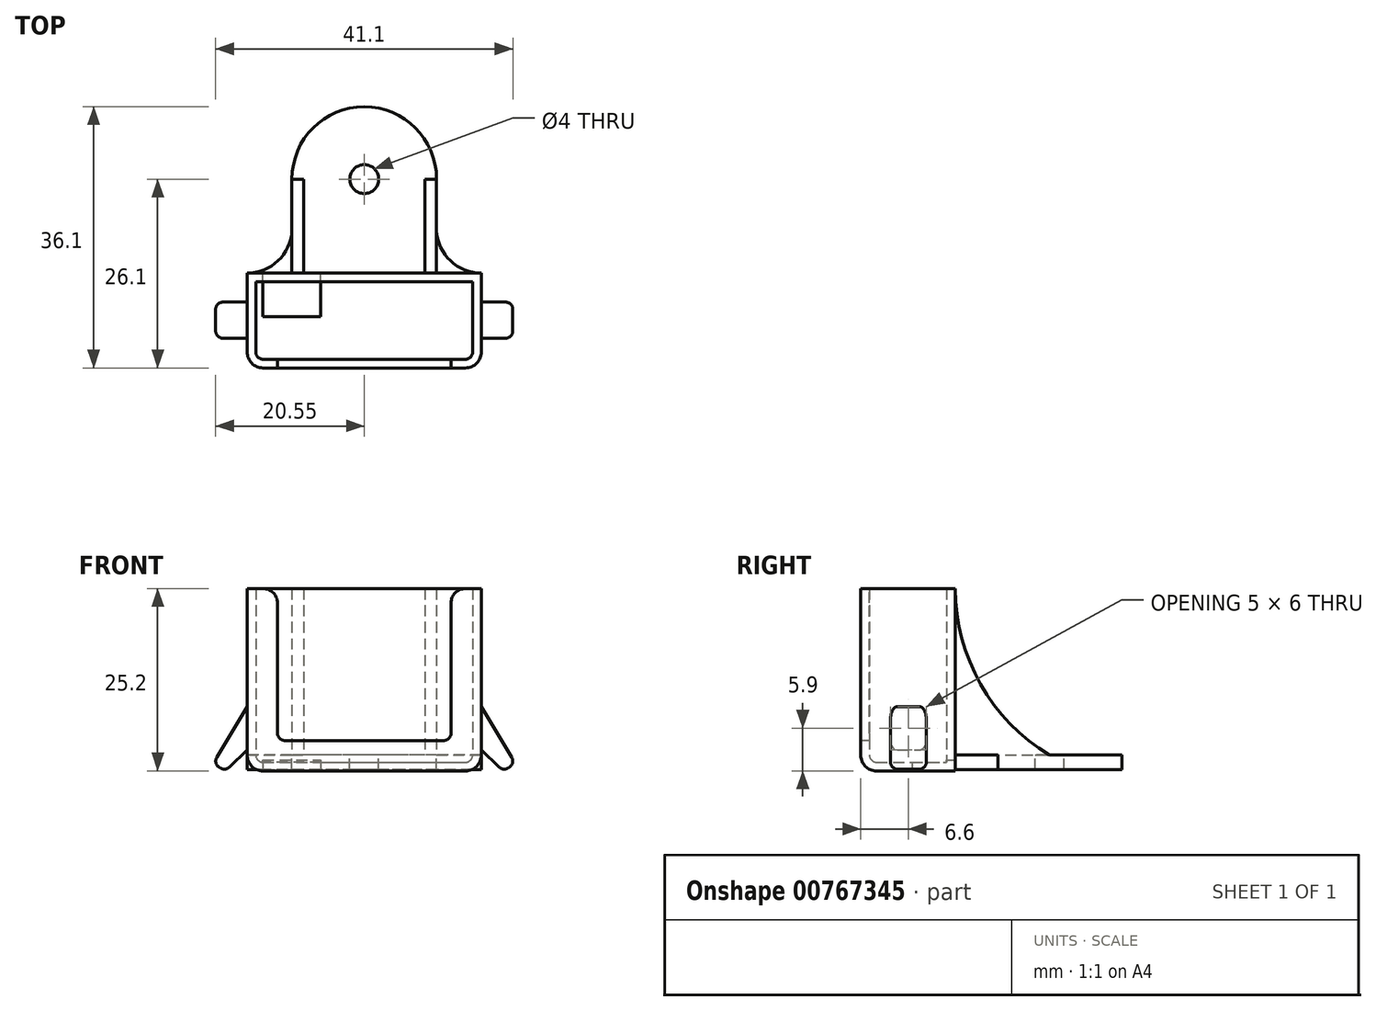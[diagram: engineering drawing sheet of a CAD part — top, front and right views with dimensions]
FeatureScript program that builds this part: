
annotation { "Feature Type Name" : "Feature", "Feature Type Description" : "" }
export const myFeature = defineFeature(function(context is Context, id is Id, definition is map)
    precondition{}
    {
        {
            var Q0;
            Q0=qCreatedBy(makeId("Front.planeOp"),FACE);
            var sketch = newSketch(context, id + "F0", { "sketchPlane" : qUnion([Q0])});
            skLineSegment(sketch, "E0.bottom", {"start": v(-15, 5) * mm, "end": v(15, 5) * mm});
            skLineSegment(sketch, "E0.top", {"start": v(-15, -20) * mm, "end": v(15, -20) * mm});
            skLineSegment(sketch, "E0.left", {"start": v(-15, 5) * mm, "end": v(-15, -20) * mm});
            skLineSegment(sketch, "E0.right", {"start": v(15, 5) * mm, "end": v(15, -20) * mm});
            skPoint(sketch, "E0.middle", {"position": v(0, -7.5) * mm});
            skPoint(sketch, "E1.visualSharp", {"position": v(-15, 5) * mm});
            skSolve(sketch);
        }
        {
            var Q0;
            Q0=qSketchRegion(id+"F0",true);
            extrude(context, id + "F1", {"entities" : qUnion([Q0]), "depth" : 10.7 * mm, "offsetDistance" : 25 * mm});
        }
        {
            var Q0;
            Q0=makeQuery(id+"F1.opExtrude","SWEPT_EDGE",EDGE,{"disambiguationData":[OSD([sQuery(id+"F0.wireOp",EDGE,"E0.bottom"),sQuery(id+"F0.wireOp",EDGE,"E0.right")])]});
            var Q1;
            Q1=makeQuery(id+"F1.opExtrude","SWEPT_EDGE",EDGE,{"disambiguationData":[OSD([sQuery(id+"F0.wireOp",EDGE,"E0.bottom"),sQuery(id+"F0.wireOp",EDGE,"E0.left")])]});
            var Q2;
            Q2=makeQuery(id+"F1.opExtrude","SWEPT_EDGE",EDGE,{"disambiguationData":[OSD([sQuery(id+"F0.wireOp",EDGE,"E0.top"),sQuery(id+"F0.wireOp",EDGE,"E0.left")])]});
            var Q3;
            Q3=makeQuery(id+"F1.opExtrude","SWEPT_EDGE",EDGE,{"disambiguationData":[OSD([sQuery(id+"F0.wireOp",EDGE,"E0.top"),sQuery(id+"F0.wireOp",EDGE,"E0.right")])]});
            var Q4;
            Q4=makeQuery(id+"F1.opExtrude","CAP_FACE",FACE,{"disambiguationData":[OSD([sQuery(id+"F0.wireOp",EDGE,"E0.bottom"),sQuery(id+"F0.wireOp",EDGE,"E0.top"),sQuery(id+"F0.wireOp",EDGE,"E0.left"),sQuery(id+"F0.wireOp",EDGE,"E0.right")])],"isStart":false});
            fillet(context, id + "F2", {"entities" : qUnion([Q0, Q1, Q2, Q3, Q4]), "radius" : 1 * mm, "tangentPropagation" : true, "allowEdgeOverflow" : false});
        }
        {
            var Q0;
            Q0=makeQuery(id+"F1.opExtrude","SWEPT_FACE",FACE,{"disambiguationData":[OSD([sQuery(id+"F0.wireOp",EDGE,"E0.bottom")])]});
            var Q1;
            Q1=makeQuery(id+"F2.opFillet","BLEND_FACE",FACE,{"disambiguationData":[OSD([sQuery(id+"F0.wireOp",EDGE,"E0.bottom")])]});
            shell(context, id + "F3", {"entities" : qUnion([Q0, Q1]), "thickness" : 1.2 * mm, "oppositeDirection" : true});
        }
        {
            var Q0;
            Q0=makeQuery(id+"F1.opExtrude","CAP_FACE",FACE,{"disambiguationData":[OSD([sQuery(id+"F0.wireOp",EDGE,"E0.bottom"),sQuery(id+"F0.wireOp",EDGE,"E0.top"),sQuery(id+"F0.wireOp",EDGE,"E0.left"),sQuery(id+"F0.wireOp",EDGE,"E0.right")])],"isStart":false});
            var sketch = newSketch(context, id + "F4", { "sketchPlane" : qUnion([Q0])});
            skLineSegment(sketch, "E2.bottom", {"start": v(-11, -17) * mm, "end": v(11, -17) * mm});
            skLineSegment(sketch, "E2.top", {"start": v(-12, 15) * mm, "end": v(12, 15) * mm});
            skLineSegment(sketch, "E2.left", {"start": v(-12, -16) * mm, "end": v(-12, 15) * mm});
            skLineSegment(sketch, "E2.right", {"start": v(12, -16) * mm, "end": v(12, 15) * mm});
            skPoint(sketch, "E3.visualSharp", {"position": v(-12, -17) * mm});
            skArc(sketch, "E3.filletArc", {"start": v(-12, -16) * mm, "mid": v(-11.7, -16.7) * mm, "end": v(-11, -17) * mm});
            skPoint(sketch, "E4.visualSharp", {"position": v(12, -17) * mm});
            skArc(sketch, "E4.filletArc", {"start": v(11, -17) * mm, "mid": v(11.7, -16.7) * mm, "end": v(12, -16) * mm});
            skLineSegment(sketch, "E5.bottom", {"start": v(-16.5, 7.5) * mm, "end": v(16.5, 7.5) * mm});
            skLineSegment(sketch, "E5.top", {"start": v(-16.5, 4) * mm, "end": v(16.5, 4) * mm});
            skLineSegment(sketch, "E5.left", {"start": v(-16.5, 7.5) * mm, "end": v(-16.5, 4) * mm});
            skLineSegment(sketch, "E5.right", {"start": v(16.5, 7.5) * mm, "end": v(16.5, 4) * mm});
            skSolve(sketch);
        }
        {
            var Q0;
            Q0=makeQuery(id+"F4.imprint","IMPRINT",FACE,{"disambiguationData":[TD([[makeQuery(id+"F4.imprint","IMPRINT",EDGE,{"derivedFrom":sQuery(id+"F4.wireOp",EDGE,"E2.bottom")}),1.0]])]});
            var Q1;
            {var subQ0=sQuery(id+"F4.wireOp",EDGE,"E5.bottom");var subQ1=sQuery(id+"F4.wireOp",EDGE,"E2.left");var subQ2=makeQuery(id+"F4.imprint","INTERSECT",VERTEX,{"derivedFrom":[subQ1,subQ0]});Q1=makeQuery(id+"F4.imprint","IMPRINT",FACE,{"disambiguationData":[TD([[makeQuery(id+"F4.imprint","IMPRINT",EDGE,{"disambiguationData":[TD([[subQ2,1.0]])],"derivedFrom":subQ1}),-1.0]])]});}
            var Q2;
            {var subQ0=sQuery(id+"F4.wireOp",EDGE,"E2.top");Q2=makeQuery(id+"F4.imprint","IMPRINT",FACE,{"disambiguationData":[TD([[makeQuery(id+"F4.imprint","IMPRINT",EDGE,{"derivedFrom":subQ0}),-1.0]])]});}
            extrude(context, id + "F5", {"entities" : qUnion([Q0, Q1, Q2]), "operationType" : NewBodyOperationType.REMOVE, "oppositeDirection" : true, "depth" : 3 * mm, "offsetDistance" : 25 * mm});
        }
        {
            var Q0;
            {var subQ8=sQuery(id+"F4.wireOp",EDGE,"E5.left");Q0=makeQuery(id+"F4.imprint","IMPRINT",FACE,{"disambiguationData":[TD([[makeQuery(id+"F4.imprint","IMPRINT",EDGE,{"derivedFrom":subQ8}),1.0]])]});}
            var Q1;
            {var subQ0=sQuery(id+"F4.wireOp",EDGE,"E5.bottom");var subQ1=sQuery(id+"F4.wireOp",EDGE,"E2.left");var subQ2=makeQuery(id+"F4.imprint","INTERSECT",VERTEX,{"derivedFrom":[subQ1,subQ0]});Q1=makeQuery(id+"F4.imprint","IMPRINT",FACE,{"disambiguationData":[TD([[makeQuery(id+"F4.imprint","IMPRINT",EDGE,{"disambiguationData":[TD([[subQ2,1.0]])],"derivedFrom":subQ1}),-1.0]])]});}
            var Q2;
            {var subQ6=sQuery(id+"F4.wireOp",EDGE,"E5.right");Q2=makeQuery(id+"F4.imprint","IMPRINT",FACE,{"disambiguationData":[TD([[makeQuery(id+"F4.imprint","IMPRINT",EDGE,{"derivedFrom":subQ6}),-1.0]])]});}
            extrude(context, id + "F6", {"entities" : qUnion([Q0, Q1, Q2]), "operationType" : NewBodyOperationType.REMOVE, "oppositeDirection" : true, "depth" : 25 * mm, "offsetDistance" : 25 * mm});
        }
        {
            var Q0;
            {var subQ0=sQuery(id+"F0.wireOp",EDGE,"E0.right");var subQ1=sQuery(id+"F0.wireOp",EDGE,"E0.left");var subQ2=sQuery(id+"F0.wireOp",EDGE,"E0.top");var subQ3=sQuery(id+"F0.wireOp",EDGE,"E0.bottom");Q0=makeQuery(id+"F5.boolean.opBoolean","INTERSECT",EDGE,{"derivedFrom":[makeQuery(id+"F3.opShell","OFFSET_FACE",FACE,{"disambiguationData":[OSD([subQ3,subQ2,subQ1,subQ0]),TDD([makeQuery(id+"F2.opFillet","BLEND_EDGE",EDGE,{"blendedFrom":[makeQuery(id+"F1.opExtrude","CAP_EDGE",EDGE,{"disambiguationData":[OSD([subQ3])],"isStart":false}),makeQuery(id+"F1.opExtrude","CAP_FACE",FACE,{"disambiguationData":[OSD([subQ3,subQ2,subQ1,subQ0])],"isStart":false})],"blendedInto":[makeQuery(id+"F1.opExtrude","CAP_FACE",FACE,{"disambiguationData":[OSD([subQ3,subQ2,subQ1,subQ0])],"isStart":false})]})])]}),makeQuery(id+"F5.opExtrude","SWEPT_FACE",FACE,{"disambiguationData":[OSD([sQuery(id+"F4.wireOp",EDGE,"E2.right")])]})]});}
            var Q1;
            {var subQ0=sQuery(id+"F0.wireOp",EDGE,"E0.right");var subQ1=sQuery(id+"F0.wireOp",EDGE,"E0.left");var subQ2=sQuery(id+"F0.wireOp",EDGE,"E0.top");var subQ3=sQuery(id+"F0.wireOp",EDGE,"E0.bottom");Q1=makeQuery(id+"F5.boolean.opBoolean","INTERSECT",EDGE,{"derivedFrom":[makeQuery(id+"F3.opShell","OFFSET_FACE",FACE,{"disambiguationData":[OSD([subQ3,subQ2,subQ1,subQ0]),TDD([makeQuery(id+"F2.opFillet","BLEND_EDGE",EDGE,{"blendedFrom":[makeQuery(id+"F1.opExtrude","CAP_EDGE",EDGE,{"disambiguationData":[OSD([subQ3])],"isStart":false}),makeQuery(id+"F1.opExtrude","CAP_FACE",FACE,{"disambiguationData":[OSD([subQ3,subQ2,subQ1,subQ0])],"isStart":false})],"blendedInto":[makeQuery(id+"F1.opExtrude","CAP_FACE",FACE,{"disambiguationData":[OSD([subQ3,subQ2,subQ1,subQ0])],"isStart":false})]})])]}),makeQuery(id+"F5.opExtrude","SWEPT_FACE",FACE,{"disambiguationData":[OSD([sQuery(id+"F4.wireOp",EDGE,"E2.left")])]})]});}
            fillet(context, id + "F7", {"entities" : qUnion([Q0, Q1]), "radius" : 2 * mm, "tangentPropagation" : true, "allowEdgeOverflow" : false});
        }
        {
            var Q0;
            Q0=makeQuery(id+"F1.opExtrude","CAP_FACE",FACE,{"disambiguationData":[OSD([sQuery(id+"F0.wireOp",EDGE,"E0.bottom"),sQuery(id+"F0.wireOp",EDGE,"E0.top"),sQuery(id+"F0.wireOp",EDGE,"E0.left"),sQuery(id+"F0.wireOp",EDGE,"E0.right")])],"isStart":true});
            var sketch = newSketch(context, id + "F8", { "sketchPlane" : qUnion([Q0])});
            skLineSegment(sketch, "E6.bottom", {"start": v(6, -19.7) * mm, "end": v(14, -19.7) * mm});
            skLineSegment(sketch, "E6.top", {"start": v(6, -24.7) * mm, "end": v(14, -24.7) * mm});
            skLineSegment(sketch, "E6.left", {"start": v(6, -19.7) * mm, "end": v(6, -24.7) * mm});
            skLineSegment(sketch, "E6.right", {"start": v(14, -19.7) * mm, "end": v(14, -24.7) * mm});
            skSolve(sketch);
        }
        {
            var Q0;
            Q0=qSketchRegion(id+"F8",true);
            extrude(context, id + "F9", {"entities" : qUnion([Q0]), "operationType" : NewBodyOperationType.REMOVE, "oppositeDirection" : true, "depth" : 6 * mm, "offsetDistance" : 25 * mm});
        }
        {
            var Q0;
            Q0=qCreatedBy(makeId("Top.planeOp"),FACE);
            var sketch = newSketch(context, id + "F10", { "sketchPlane" : qUnion([Q0])});
            skLineSegment(sketch, "E7.bottom", {"start": v(-10, 1.2) * mm, "end": v(10, 1.2) * mm});
            skLineSegment(sketch, "E7.top", {"start": v(0, 24.2) * mm, "end": v(0, 24.2) * mm});
            skLineSegment(sketch, "E7.left", {"start": v(-10, 1.2) * mm, "end": v(-10, 14.2) * mm});
            skLineSegment(sketch, "E7.right", {"start": v(10, 1.2) * mm, "end": v(10, 14.2) * mm});
            skPoint(sketch, "E8.visualSharp", {"position": v(-10, 24.2) * mm});
            skArc(sketch, "E8.filletArc", {"start": v(0, 24.2) * mm, "mid": v(-7.07, 21.27) * mm, "end": v(-10, 14.2) * mm});
            skPoint(sketch, "E9.visualSharp", {"position": v(10, 24.2) * mm});
            skArc(sketch, "E9.filletArc", {"start": v(10, 14.2) * mm, "mid": v(7.07, 21.27) * mm, "end": v(0, 24.2) * mm});
            skCircle(sketch, "E10", {"center": v(0, 14.2) * mm, "radius": 2 * mm});
            skLineSegment(sketch, "E11", {"start": v(-10, 1.2) * mm, "end": v(-16.2, 1.2) * mm});
            skLineSegment(sketch, "E12", {"start": v(10, 1.2) * mm, "end": v(16.2, 1.2) * mm});
            skArc(sketch, "E13", {"start": v(-16.2, 1.2) * mm, "mid": v(-11.7, 3.12) * mm, "end": v(-10, 7.7) * mm});
            skArc(sketch, "E14", {"start": v(10, 7.7) * mm, "mid": v(11.7, 3.12) * mm, "end": v(16.2, 1.2) * mm});
            skSolve(sketch);
        }
        {
            var Q0;
            Q0=qSketchRegion(id+"F10",true);
            extrude(context, id + "F11", {"entities" : qUnion([Q0]), "operationType" : NewBodyOperationType.ADD, "oppositeDirection" : true, "depth" : 21 * mm, "offsetDistance" : 25 * mm, "hasSecondDirection" : true, "secondDirectionOppositeDirection" : true, "secondDirectionDepth" : 19 * mm});
        }
        {
            var Q0;
            {var subQ2=sQuery(id+"F0.wireOp",EDGE,"E0.right");var subQ3=sQuery(id+"F0.wireOp",EDGE,"E0.top");var subQ4=sQuery(id+"F0.wireOp",EDGE,"E0.left");Q0=makeQuery(id+"F11.boolean.opBoolean","SPLIT",FACE,{"disambiguationData":[TD([makeQuery(id+"F1.opExtrude","SWEPT_FACE",FACE,{"disambiguationData":[OSD([subQ3])]})])],"derivedFrom":makeQuery(id+"F1.opExtrude","CAP_FACE",FACE,{"disambiguationData":[OSD([sQuery(id+"F0.wireOp",EDGE,"E0.bottom"),subQ3,subQ4,subQ2])],"isStart":true})});}
            var sketch = newSketch(context, id + "F12", { "sketchPlane" : qUnion([Q0])});
            skLineSegment(sketch, "E15", {"start": v(16.2, -12.3) * mm, "end": v(20.4, -19.33) * mm});
            skLineSegment(sketch, "E16", {"start": v(20.06, -20.7) * mm, "end": v(19.86, -20.82) * mm});
            skLineSegment(sketch, "E17", {"start": v(18.65, -20.68) * mm, "end": v(16.2, -18.3) * mm});
            skLineSegment(sketch, "E18", {"start": v(16.2, -18.3) * mm, "end": v(16.2, -12.3) * mm});
            skPoint(sketch, "E19.visualSharp", {"position": v(20.92, -20.2) * mm});
            skArc(sketch, "E19.filletArc", {"start": v(20.06, -20.7) * mm, "mid": v(20.52, -20.1) * mm, "end": v(20.4, -19.33) * mm});
            skPoint(sketch, "E20.visualSharp", {"position": v(19.2, -21.22) * mm});
            skArc(sketch, "E20.filletArc", {"start": v(18.65, -20.68) * mm, "mid": v(19.23, -20.96) * mm, "end": v(19.86, -20.82) * mm});
            skLineSegment(sketch, "E21.MirrorCS", {"start": v(-20.06, -20.7) * mm, "end": v(-19.86, -20.82) * mm});
            skArc(sketch, "E22.MirrorCS", {"start": v(-20.06, -20.7) * mm, "mid": v(-20.52, -20.1) * mm, "end": v(-20.4, -19.33) * mm});
            skArc(sketch, "E23.MirrorCS", {"start": v(-18.65, -20.68) * mm, "mid": v(-19.23, -20.96) * mm, "end": v(-19.86, -20.82) * mm});
            skPoint(sketch, "E24.MirrorP", {"position": v(-20.92, -20.2) * mm});
            skPoint(sketch, "E25.MirrorP", {"position": v(-19.2, -21.22) * mm});
            skLineSegment(sketch, "E26.MirrorCS", {"start": v(-16.2, -18.3) * mm, "end": v(-16.2, -12.3) * mm});
            skLineSegment(sketch, "E27.MirrorCS", {"start": v(-18.65, -20.68) * mm, "end": v(-16.2, -18.3) * mm});
            skLineSegment(sketch, "E28.MirrorCS", {"start": v(-16.2, -12.3) * mm, "end": v(-20.4, -19.33) * mm});
            skSolve(sketch);
        }
        {
            var Q0;
            Q0=qSketchRegion(id+"F12",true);
            extrude(context, id + "F13", {"entities" : qUnion([Q0]), "operationType" : NewBodyOperationType.ADD, "oppositeDirection" : true, "depth" : 9 * mm, "offsetDistance" : 25 * mm, "hasSecondDirection" : true, "secondDirectionOppositeDirection" : true, "secondDirectionDepth" : 4 * mm});
        }
        {
            var Q0;
            Q0=makeQuery(id+"F13.opExtrude","CAP_EDGE",EDGE,{"disambiguationData":[OSD([sQuery(id+"F12.wireOp",EDGE,"E15")])],"isStart":true});
            var Q1;
            Q1=makeQuery(id+"F13.opExtrude","CAP_EDGE",EDGE,{"disambiguationData":[OSD([sQuery(id+"F12.wireOp",EDGE,"E15")])],"isStart":false});
            var Q2;
            Q2=makeQuery(id+"F13.opExtrude","CAP_EDGE",EDGE,{"disambiguationData":[OSD([sQuery(id+"F12.wireOp",EDGE,"E28.MirrorCS")])],"isStart":false});
            var Q3;
            Q3=makeQuery(id+"F13.opExtrude","CAP_EDGE",EDGE,{"disambiguationData":[OSD([sQuery(id+"F12.wireOp",EDGE,"E28.MirrorCS")])],"isStart":true});
            fillet(context, id + "F14", {"entities" : qUnion([Q0, Q1, Q2, Q3]), "radius" : 1 * mm, "tangentPropagation" : true, "allowEdgeOverflow" : false});
        }
        {
            var Q0;
            Q0=qCreatedBy(makeId("Right.planeOp"),FACE);
            var sketch = newSketch(context, id + "F15", { "sketchPlane" : qUnion([Q0])});
            skArc(sketch, "E29", {"start": v(1.2, 4) * mm, "mid": v(4.67, -9.2) * mm, "end": v(14.2, -19) * mm});
            skLineSegment(sketch, "E30", {"start": v(1.2, 4) * mm, "end": v(1.2, -19) * mm});
            skLineSegment(sketch, "E31", {"start": v(1.2, -19) * mm, "end": v(14.2, -19) * mm});
            skSolve(sketch);
        }
        {
            var Q0;
            Q0=makeQuery(id+"F15.imprint","IMPRINT",FACE,{"disambiguationData":[TD([[makeQuery(id+"F15.imprint","IMPRINT",EDGE,{"derivedFrom":sQuery(id+"F15.wireOp",EDGE,"E29")}),-1.0]])]});
            extrude(context, id + "F16", {"entities" : qUnion([Q0]), "operationType" : NewBodyOperationType.ADD, "depth" : 10 * mm, "offsetDistance" : 25 * mm, "hasSecondDirection" : true, "secondDirectionOppositeDirection" : false, "secondDirectionDepth" : 8.4 * mm});
        }
        {
            var Q0;
            Q0=makeQuery(id+"F15.imprint","IMPRINT",FACE,{"disambiguationData":[TD([[makeQuery(id+"F15.imprint","IMPRINT",EDGE,{"derivedFrom":sQuery(id+"F15.wireOp",EDGE,"E29")}),-1.0]])]});
            extrude(context, id + "F17", {"entities" : qUnion([Q0]), "operationType" : NewBodyOperationType.ADD, "oppositeDirection" : true, "depth" : 10 * mm, "offsetDistance" : 25 * mm, "hasSecondDirection" : true, "secondDirectionOppositeDirection" : true, "secondDirectionDepth" : 8.4 * mm});
        }
    });
